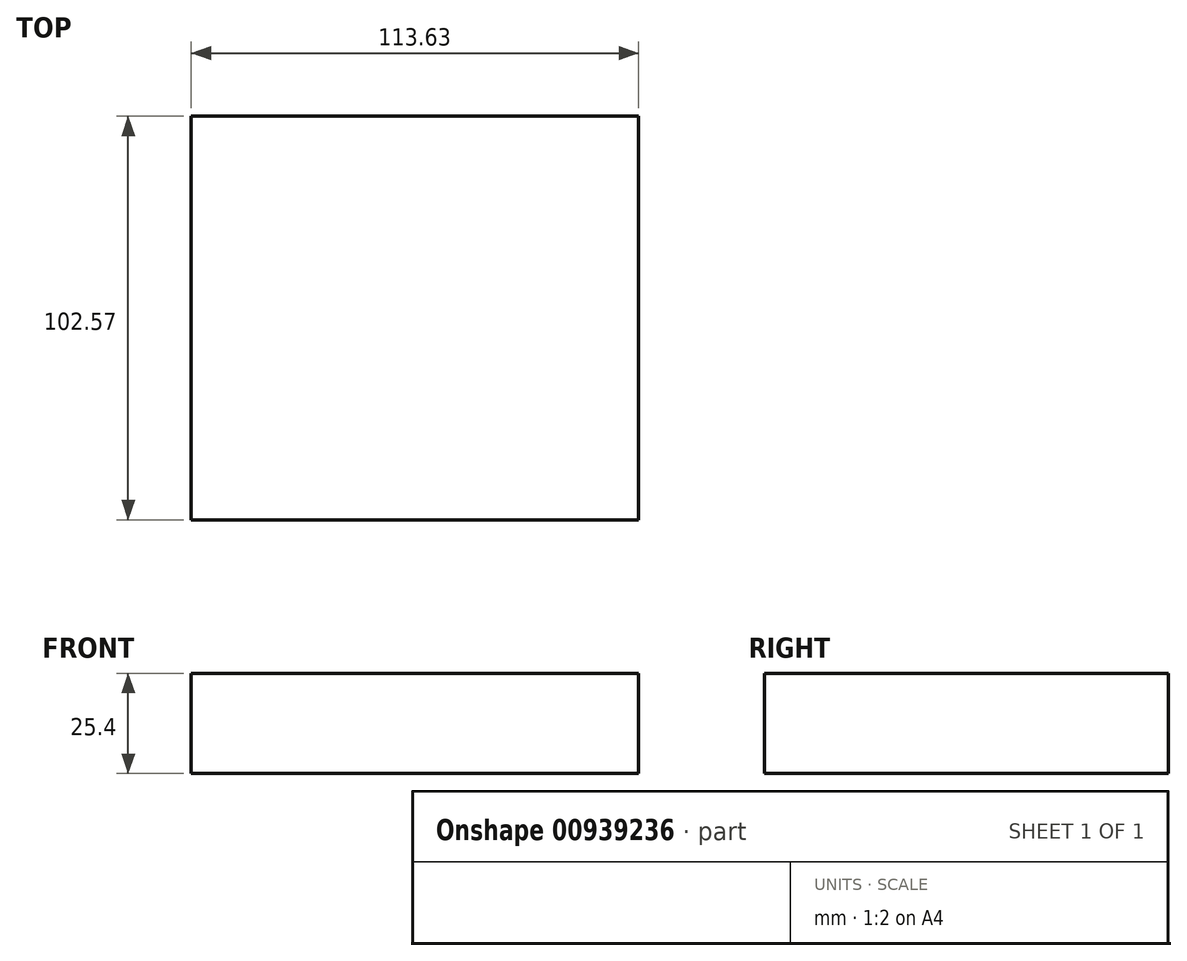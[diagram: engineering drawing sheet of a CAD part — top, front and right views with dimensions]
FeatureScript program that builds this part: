
annotation { "Feature Type Name" : "Feature", "Feature Type Description" : "" }
export const myFeature = defineFeature(function(context is Context, id is Id, definition is map)
    precondition{}
    {
        {
            var Q0;
            Q0=qCreatedBy(makeId("Top.planeOp"),FACE);
            var sketch = newSketch(context, id + "F0", { "sketchPlane" : qUnion([Q0])});
            skLineSegment(sketch, "E0.bottom", {"start": v(-54.36, 48.75) * mm, "end": v(59.27, 48.75) * mm});
            skLineSegment(sketch, "E0.top", {"start": v(-54.36, -53.82) * mm, "end": v(59.27, -53.82) * mm});
            skLineSegment(sketch, "E0.left", {"start": v(-54.36, 48.75) * mm, "end": v(-54.36, -53.82) * mm});
            skLineSegment(sketch, "E0.right", {"start": v(59.27, 48.75) * mm, "end": v(59.27, -53.82) * mm});
            skSolve(sketch);
        }
        {
            var Q0;
            Q0 = qSketchRegion(id + "F0", true);
            extrude(context, id + "F1", {"entities" : qUnion([Q0]), "depth" : 25.4 * mm, "offsetDistance" : 25.4 * mm});
        }
    });
